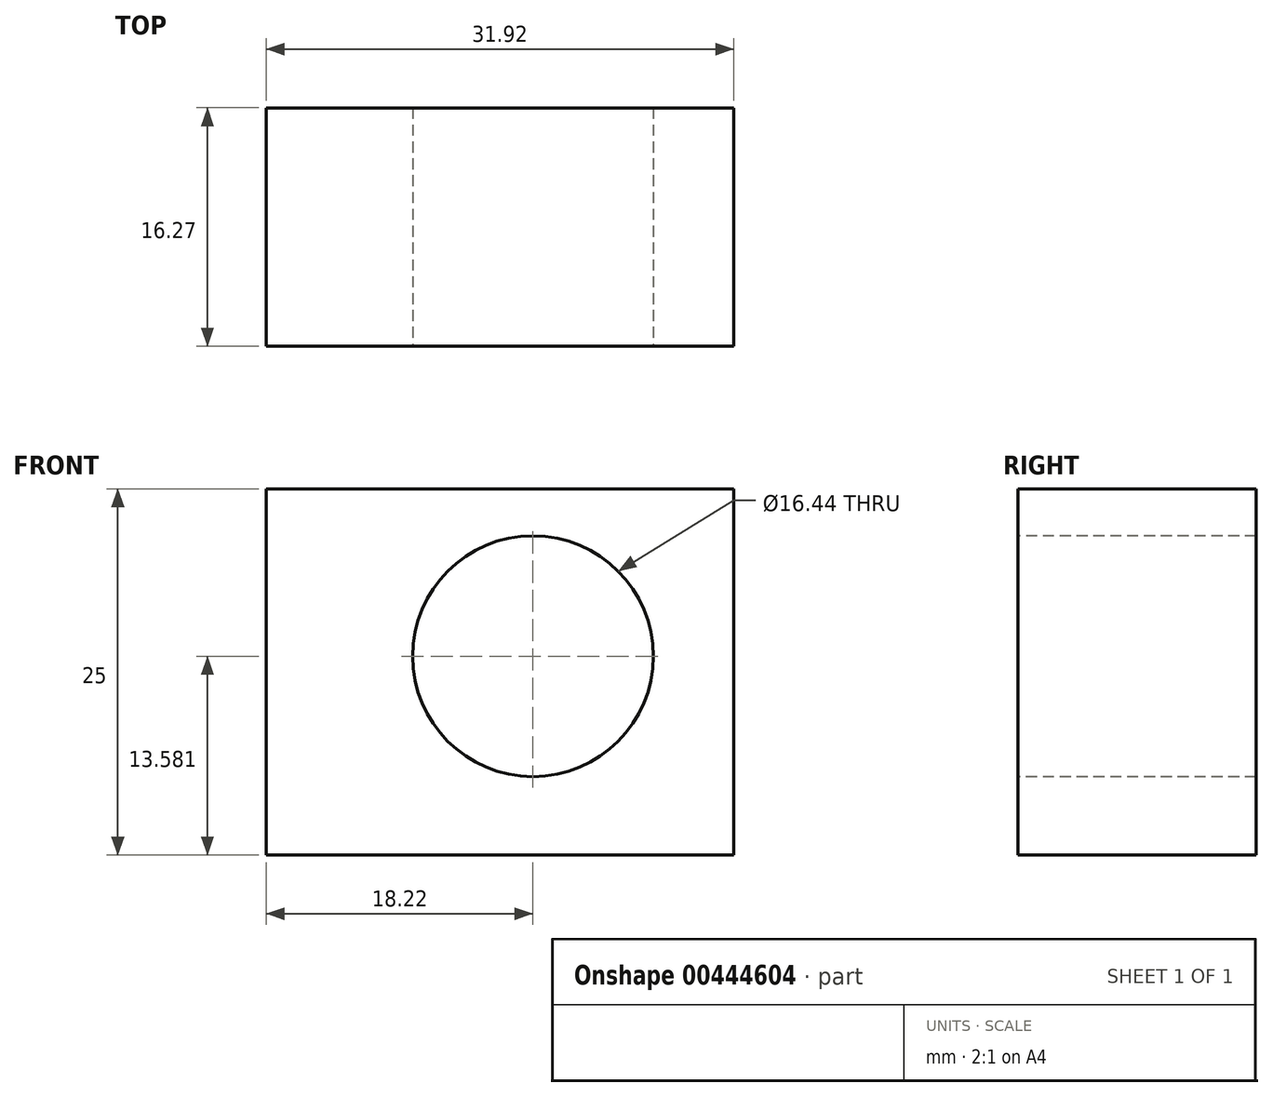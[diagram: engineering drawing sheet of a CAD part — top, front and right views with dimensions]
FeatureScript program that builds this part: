
annotation { "Feature Type Name" : "Feature", "Feature Type Description" : "" }
export const myFeature = defineFeature(function(context is Context, id is Id, definition is map)
    precondition{}
    {
        {
            var Q0;
            Q0=qCreatedBy(makeId("Top.planeOp"),FACE);
            var sketch = newSketch(context, id + "F0", { "sketchPlane" : qUnion([Q0])});
            skLineSegment(sketch, "E0.bottom", {"start": v(-30.5, 21.86) * mm, "end": v(1.42, 21.86) * mm});
            skLineSegment(sketch, "E0.top", {"start": v(-30.5, 5.6) * mm, "end": v(1.42, 5.6) * mm});
            skLineSegment(sketch, "E0.left", {"start": v(-30.5, 21.86) * mm, "end": v(-30.5, 5.6) * mm});
            skLineSegment(sketch, "E0.right", {"start": v(1.42, 21.86) * mm, "end": v(1.42, 5.6) * mm});
            skSolve(sketch);
        }
        {
            var Q0;
            Q0=makeQuery(id+"F0.imprint","IMPRINT",FACE,{"disambiguationData":[TD([[makeQuery(id+"F0.imprint","IMPRINT",EDGE,{"derivedFrom":sQuery(id+"F0.wireOp",EDGE,"E0.bottom")}),-1.0]])]});
            extrude(context, id + "F1", {"entities" : qUnion([Q0]), "depth" : 25 * mm});
        }
        {
            var Q0;
            Q0=makeQuery(id+"F1.opExtrude","SWEPT_FACE",FACE,{"disambiguationData":[OSD([sQuery(id+"F0.wireOp",EDGE,"E0.top")])]});
            var sketch = newSketch(context, id + "F2", { "sketchPlane" : qUnion([Q0])});
            skCircle(sketch, "E1", {"center": v(-12.28, 13.58) * mm, "radius": 8.22 * mm});
            skSolve(sketch);
        }
        {
            var Q0;
            Q0 = qSketchRegion(id + "F2", true);
            extrude(context, id + "F3", {"entities" : qUnion([Q0]), "operationType" : NewBodyOperationType.REMOVE, "oppositeDirection" : true, "depth" : 25 * mm});
        }
    });
